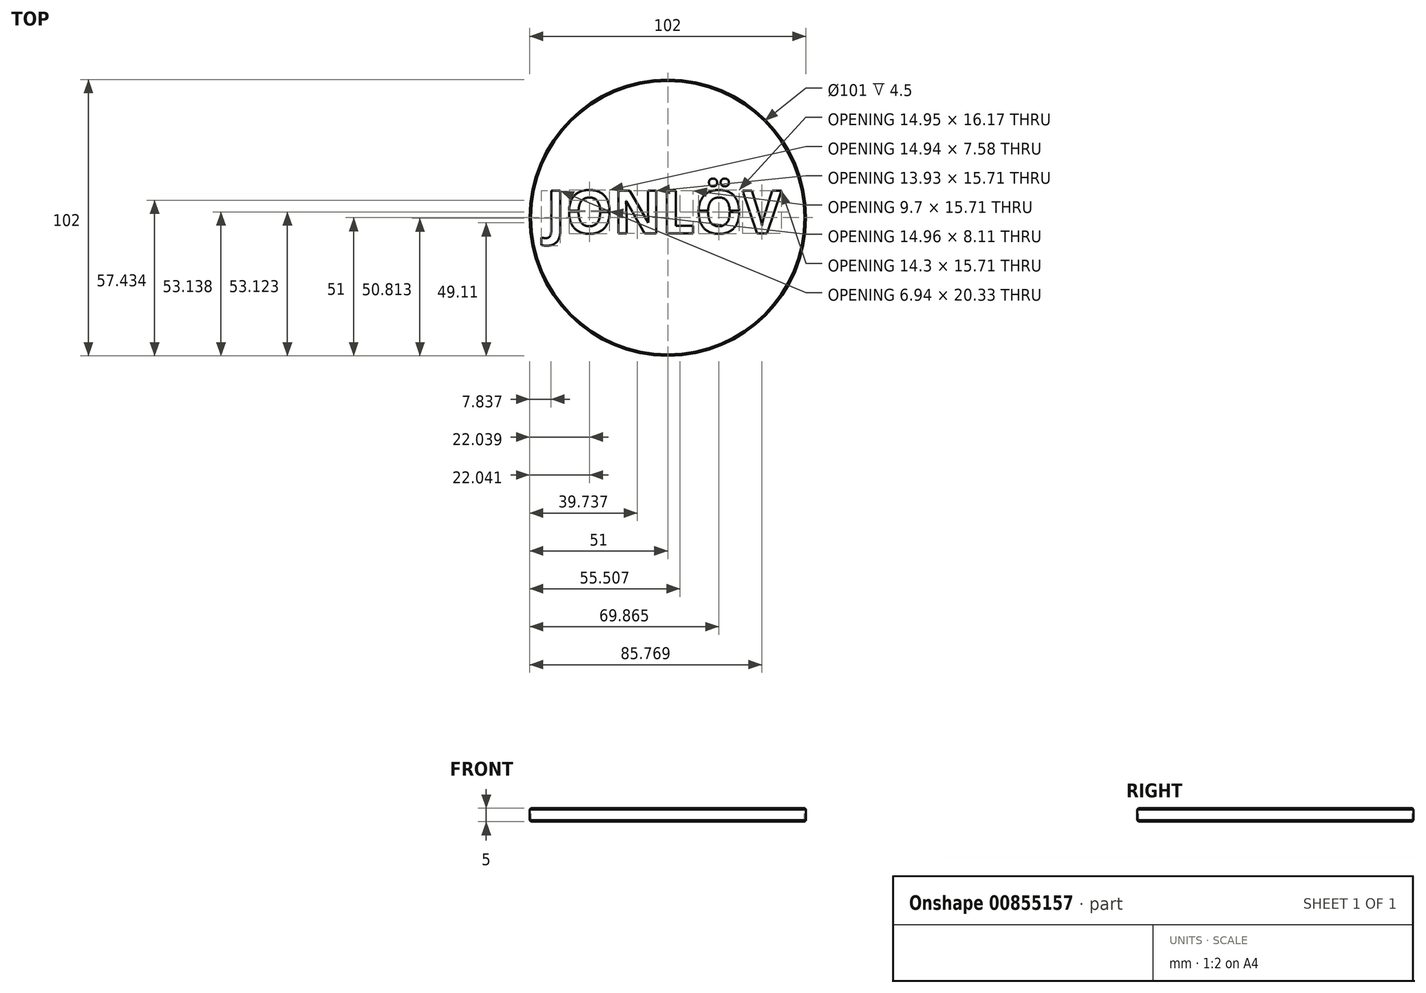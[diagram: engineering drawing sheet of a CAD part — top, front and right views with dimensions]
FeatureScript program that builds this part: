
annotation { "Feature Type Name" : "Feature", "Feature Type Description" : "" }
export const myFeature = defineFeature(function(context is Context, id is Id, definition is map)
    precondition{}
    {
        {
            var Q0;
            Q0=qCreatedBy(makeId("Top.planeOp"),FACE);
            var sketch = newSketch(context, id + "F0", { "sketchPlane" : qUnion([Q0])});
            skCircle(sketch, "E0", {"center": v(0, 0) * mm, "radius": 50 * mm});
            skCircle(sketch, "E1.0", {"center": v(0, 0) * mm, "radius": 50.5 * mm});
            skSolve(sketch);
        }
        {
            var Q0;
            Q0 = qSketchRegion(id + "F0", true);
            var Q1;
            Q1=makeQuery(id+"F0.imprint","IMPRINT",FACE,{"disambiguationData":[TD([[makeQuery(id+"F0.imprint","IMPRINT",EDGE,{"derivedFrom":sQuery(id+"F0.wireOp",EDGE,"E0")}),1.0]])]});
            extrude(context, id + "F1", {"entities" : qUnion([Q0, Q1]), "depth" : 0.5 * mm, "offsetDistance" : 25 * mm});
        }
        {
            var Q0;
            Q0=makeQuery(id+"F1.opExtrude","CAP_FACE",FACE,{"disambiguationData":[OSD([sQuery(id+"F0.wireOp",EDGE,"E1.0")])],"isStart":false});
            var sketch = newSketch(context, id + "F2", { "sketchPlane" : qUnion([Q0])});
            skText(sketch, "E2", { "text": "JONLÖV", "fontName": "OpenSans-Bold.ttf"});
            const initialGuessF2  = {"E2": [-0.045, -0.00573, 1, 0, 0.01584]};
            skSetInitialGuess(sketch, initialGuessF2);
            skSolve(sketch);
        }
        {
            var Q0;
            Q0 = qSketchRegion(id + "F2", true);
            extrude(context, id + "F3", {"entities" : qUnion([Q0]), "operationType" : NewBodyOperationType.REMOVE, "oppositeDirection" : true, "depth" : 25 * mm, "offsetDistance" : 25 * mm});
        }
        {
            var Q0;
            {var subQ30=sQuery(id+"F0.wireOp",EDGE,"E1.0");var subQ31=makeQuery(id+"F1.opExtrude","SWEPT_FACE",FACE,{"disambiguationData":[OSD([subQ30])]});Q0=makeQuery(id+"Fns4HP2ZforgTSv_1.boolean.opBoolean","SPLIT",FACE,{"disambiguationData":[TD([subQ31])],"derivedFrom":makeQuery(id+"F3.boolean.opBoolean","SPLIT",FACE,{"disambiguationData":[TD([subQ31])],"derivedFrom":makeQuery(id+"F1.opExtrude","CAP_FACE",FACE,{"disambiguationData":[OSD([subQ30])],"isStart":false})})});}
            var sketch = newSketch(context, id + "F4", { "sketchPlane" : qUnion([Q0])});
            skCircle(sketch, "E3.0", {"center": v(0, 0) * mm, "radius": 51 * mm});
            skSolve(sketch);
        }
        {
            var Q0;
            Q0=makeQuery(id+"F4.imprint","IMPRINT",FACE,{"disambiguationData":[TD([[makeQuery(id+"F4.imprint","IMPRINT",EDGE,{"derivedFrom":sQuery(id+"F4.wireOp",EDGE,"E3.0")}),1.0]])]});
            extrude(context, id + "F5", {"entities" : qUnion([Q0]), "operationType" : NewBodyOperationType.ADD, "oppositeDirection" : true, "depth" : 5 * mm, "offsetDistance" : 25 * mm});
        }
        {
            var Q0;
            Q0=makeQuery(id+"F5.opExtrude","CAP_EDGE",EDGE,{"disambiguationData":[OSD([sQuery(id+"F4.wireOp",EDGE,"E3.0")])],"isStart":true});
            var Q1;
            Q1=makeQuery(id+"F5.opExtrude","CAP_EDGE",EDGE,{"disambiguationData":[OSD([sQuery(id+"F4.wireOp",EDGE,"E3.0")])],"isStart":false});
            chamfer(context, id + "F6", {"entities" : qUnion([Q0, Q1]), "width" : 0.5 * mm, "tangentPropagation" : true});
        }
        {
            var Q0;
            {var subQ0=sQuery(id+"F0.wireOp",EDGE,"E1.0");var subQ31=makeQuery(id+"F1.opExtrude","SWEPT_FACE",FACE,{"disambiguationData":[OSD([subQ0])]});Q0=makeQuery(id+"F5.boolean.opBoolean","MERGE",FACE,{"derivedFrom":[makeQuery(id+"Fns4HP2ZforgTSv_1.boolean.opBoolean","SPLIT",FACE,{"disambiguationData":[TD([subQ31])],"derivedFrom":makeQuery(id+"F3.boolean.opBoolean","SPLIT",FACE,{"disambiguationData":[TD([subQ31])],"derivedFrom":makeQuery(id+"F1.opExtrude","CAP_FACE",FACE,{"disambiguationData":[OSD([subQ0])],"isStart":false})})}),makeQuery(id+"F5.opExtrude","CAP_FACE",FACE,{"disambiguationData":[OSD([subQ0,sQuery(id+"F4.wireOp",EDGE,"E3.0")])],"isStart":true})]});}
            var sketch = newSketch(context, id + "F7", { "sketchPlane" : qUnion([Q0])});
            skLineSegment(sketch, "E4", {"start": v(-36.43, 2.17) * mm, "end": v(-21.48, 2.15) * mm});
            skLineSegment(sketch, "E5", {"start": v(-21.48, 2.15) * mm, "end": v(-21.49, 2.65) * mm});
            skLineSegment(sketch, "E6", {"start": v(-21.49, 2.65) * mm, "end": v(-36.43, 2.65) * mm});
            skLineSegment(sketch, "E7", {"start": v(-36.43, 2.65) * mm, "end": v(-36.43, 2.17) * mm});
            skLineSegment(sketch, "E8", {"start": v(11.4, 2.17) * mm, "end": v(26.36, 2.15) * mm});
            skLineSegment(sketch, "E9", {"start": v(26.36, 2.15) * mm, "end": v(26.35, 2.65) * mm});
            skLineSegment(sketch, "E10", {"start": v(26.35, 2.65) * mm, "end": v(11.4, 2.65) * mm});
            skLineSegment(sketch, "E11", {"start": v(11.4, 2.65) * mm, "end": v(11.4, 2.17) * mm});
            skSolve(sketch);
        }
        {
            var Q0;
            Q0=makeQuery(id+"F7.imprint","IMPRINT",FACE,{"disambiguationData":[TD([[makeQuery(id+"F7.imprint","IMPRINT",EDGE,{"derivedFrom":sQuery(id+"F7.wireOp",EDGE,"E4")}),1.0]])]});
            var Q1;
            {var subQ0=sQuery(id+"F7.wireOp",EDGE,"E8");Q1=makeQuery(id+"F7.imprint","IMPRINT",FACE,{"disambiguationData":[TD([[makeQuery(id+"F7.imprint","IMPRINT",EDGE,{"derivedFrom":subQ0}),1.0]])]});}
            extrude(context, id + "F8", {"entities" : qUnion([Q0, Q1]), "operationType" : NewBodyOperationType.ADD, "oppositeDirection" : true, "depth" : 0.5 * mm, "offsetDistance" : 25 * mm});
        }
    });
